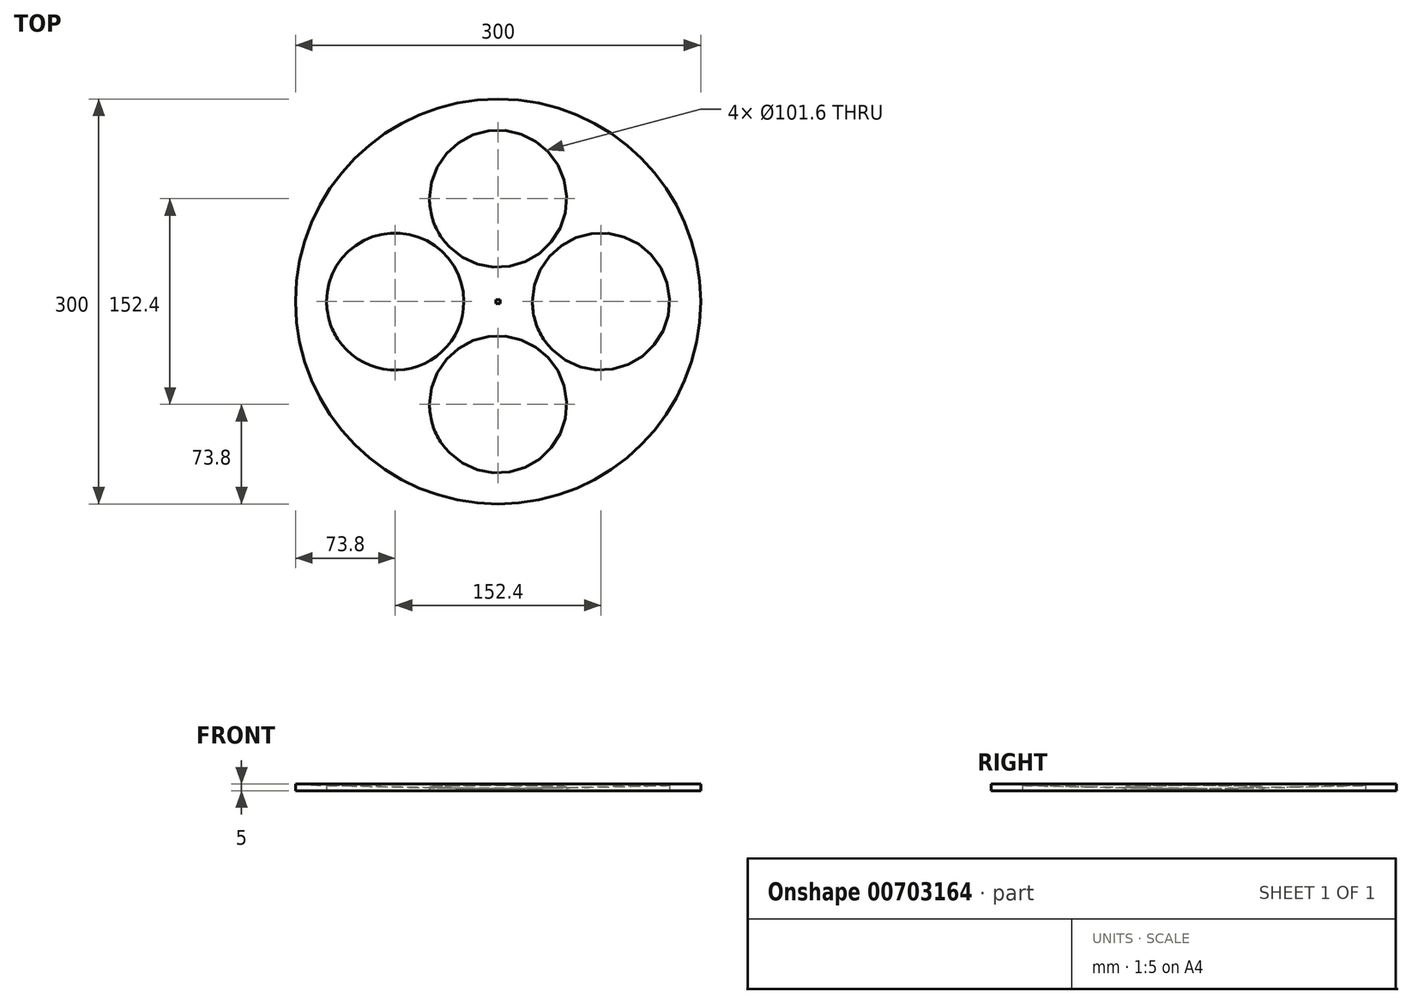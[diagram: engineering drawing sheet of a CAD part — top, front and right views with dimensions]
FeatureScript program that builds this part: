
annotation { "Feature Type Name" : "Feature", "Feature Type Description" : "" }
export const myFeature = defineFeature(function(context is Context, id is Id, definition is map)
    precondition{}
    {
        {
            var Q0;
            Q0=qCreatedBy(makeId("Right.planeOp"),FACE);
            var sketch = newSketch(context, id + "F0", { "sketchPlane" : qUnion([Q0])});
            skLineSegment(sketch, "E0", {"start": v(0, 0) * mm, "end": v(-150, 0) * mm});
            skLineSegment(sketch, "E1", {"start": v(-150, 0) * mm, "end": v(-150, 5) * mm});
            skLineSegment(sketch, "E2", {"start": v(0, 0) * mm, "end": v(0, 2) * mm});
            skArc(sketch, "E3", {"start": v(-150, 5) * mm, "mid": v(-75.02, 2.46) * mm, "end": v(0, 2) * mm});
            skSolve(sketch);
        }
        {
            var Q0;
            Q0=makeQuery(id+"F0.imprint","IMPRINT",FACE,{"disambiguationData":[TD([[makeQuery(id+"F0.imprint","IMPRINT",EDGE,{"derivedFrom":sQuery(id+"F0.wireOp",EDGE,"E0")}),-1.0]])]});
            var Q1;
            Q1=sQuery(id+"F0.wireOp",EDGE,"E2");
            revolve(context, id + "F1", {"surfaceOperationType" : NewSurfaceOperationType.NEW, "entities" : qUnion([Q0]), "axis" : qUnion([Q1]), "revolveType" : RevolveType.FULL});
        }
        {
            var Q0;
            Q0=makeQuery(id+"F1.opRevolve","SWEPT_FACE",FACE,{"disambiguationData":[OSD([sQuery(id+"F0.wireOp",EDGE,"E0")])]});
            var sketch = newSketch(context, id + "F2", { "sketchPlane" : qUnion([Q0])});
            skLineSegment(sketch, "E4", {"start": v(0, 0) * mm, "end": v(-76.2, 0) * mm});
            skLineSegment(sketch, "E5", {"start": v(0, 0) * mm, "end": v(0, 76.2) * mm});
            skLineSegment(sketch, "E6", {"start": v(0, 0) * mm, "end": v(0, -76.2) * mm});
            skLineSegment(sketch, "E7", {"start": v(0, 0) * mm, "end": v(76.2, 0) * mm});
            skLineSegment(sketch, "E8.bottom", {"start": v(1.5, 1.5) * mm, "end": v(-1.5, 1.5) * mm});
            skLineSegment(sketch, "E8.top", {"start": v(1.5, -1.5) * mm, "end": v(-1.5, -1.5) * mm});
            skLineSegment(sketch, "E8.left", {"start": v(1.5, 1.5) * mm, "end": v(1.5, -1.5) * mm});
            skLineSegment(sketch, "E8.right", {"start": v(-1.5, 1.5) * mm, "end": v(-1.5, -1.5) * mm});
            skPoint(sketch, "E8.middle", {"position": v(0, 0) * mm});
            skCircle(sketch, "E9", {"center": v(-76.2, 0) * mm, "radius": 50.8 * mm});
            skCircle(sketch, "E10", {"center": v(0, 76.2) * mm, "radius": 50.8 * mm});
            skCircle(sketch, "E11", {"center": v(76.2, 0) * mm, "radius": 50.8 * mm});
            skCircle(sketch, "E12", {"center": v(0, -76.2) * mm, "radius": 50.8 * mm});
            skSolve(sketch);
        }
        {
            var Q0;
            Q0=makeQuery(id+"F2.imprint","IMPRINT",FACE,{"disambiguationData":[TD([[makeQuery(id+"F2.imprint","IMPRINT",EDGE,{"derivedFrom":sQuery(id+"F2.wireOp",EDGE,"E12")}),1.0]])]});
            var Q1;
            Q1=makeQuery(id+"F2.imprint","IMPRINT",FACE,{"disambiguationData":[TD([[makeQuery(id+"F2.imprint","IMPRINT",EDGE,{"derivedFrom":sQuery(id+"F2.wireOp",EDGE,"E9")}),1.0]])]});
            var Q2;
            Q2=makeQuery(id+"F2.imprint","IMPRINT",FACE,{"disambiguationData":[TD([[makeQuery(id+"F2.imprint","IMPRINT",EDGE,{"derivedFrom":sQuery(id+"F2.wireOp",EDGE,"E10")}),1.0]])]});
            var Q3;
            Q3=makeQuery(id+"F2.imprint","IMPRINT",FACE,{"disambiguationData":[TD([[makeQuery(id+"F2.imprint","IMPRINT",EDGE,{"derivedFrom":sQuery(id+"F2.wireOp",EDGE,"E11")}),1.0]])]});
            var Q4;
            {var subQ3=sQuery(id+"F2.wireOp",EDGE,"E8.right");var subQ5=sQuery(id+"F2.wireOp",EDGE,"E8.bottom");var subQ6=makeQuery(id+"F2.imprint","INTERSECT",VERTEX,{"derivedFrom":[subQ5,subQ3]});Q4=makeQuery(id+"F2.imprint","IMPRINT",FACE,{"disambiguationData":[TD([[makeQuery(id+"F2.imprint","IMPRINT",EDGE,{"disambiguationData":[TD([[subQ6,1.0]])],"derivedFrom":subQ5}),1.0]])]});}
            var Q5;
            {var subQ3=sQuery(id+"F2.wireOp",EDGE,"E8.top");var subQ5=sQuery(id+"F2.wireOp",EDGE,"E8.left");var subQ7=makeQuery(id+"F2.imprint","INTERSECT",VERTEX,{"derivedFrom":[subQ3,subQ5]});Q5=makeQuery(id+"F2.imprint","IMPRINT",FACE,{"disambiguationData":[TD([[makeQuery(id+"F2.imprint","IMPRINT",EDGE,{"disambiguationData":[TD([[subQ7,-1.0]])],"derivedFrom":subQ3}),-1.0]])]});}
            var Q6;
            {var subQ3=sQuery(id+"F2.wireOp",EDGE,"E8.bottom");var subQ5=sQuery(id+"F2.wireOp",EDGE,"E8.left");var subQ7=makeQuery(id+"F2.imprint","INTERSECT",VERTEX,{"derivedFrom":[subQ3,subQ5]});Q6=makeQuery(id+"F2.imprint","IMPRINT",FACE,{"disambiguationData":[TD([[makeQuery(id+"F2.imprint","IMPRINT",EDGE,{"disambiguationData":[TD([[subQ7,-1.0]])],"derivedFrom":subQ3}),1.0]])]});}
            var Q7;
            {var subQ3=sQuery(id+"F2.wireOp",EDGE,"E8.right");var subQ5=sQuery(id+"F2.wireOp",EDGE,"E8.top");var subQ7=makeQuery(id+"F2.imprint","INTERSECT",VERTEX,{"derivedFrom":[subQ5,subQ3]});Q7=makeQuery(id+"F2.imprint","IMPRINT",FACE,{"disambiguationData":[TD([[makeQuery(id+"F2.imprint","IMPRINT",EDGE,{"disambiguationData":[TD([[subQ7,1.0]])],"derivedFrom":subQ5}),-1.0]])]});}
            extrude(context, id + "F3", {"entities" : qUnion([Q0, Q1, Q2, Q3, Q4, Q5, Q6, Q7]), "operationType" : NewBodyOperationType.REMOVE, "oppositeDirection" : true, "depth" : 25.4 * mm, "offsetDistance" : 25.4 * mm});
        }
    });
